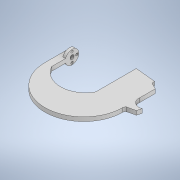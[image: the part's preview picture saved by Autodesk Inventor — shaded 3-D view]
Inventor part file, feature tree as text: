
AUTODESK INVENTOR PART (.ipt)
format: ipt  version: 2021 (Build 250183000, 183)  size: 172,032 bytes
history: native  units: in
note: dims shown in document units (in); Inventor stores cm internally (conversion verified against a paired STEP export)
features: other x3, extrude x3, sketch x3, projected_geometry x1
ambient origin geometry x8: Origin, YZ Plane, XZ Plane, XY Plane, X Axis, Y Axis, Z Axis, Center Point
bodies: Solid1 (feature_tree)
feature tree (10):
  other  "Blocks"
  extrude  "Extrusion1"  Depth=0.3937in
  extrude  "Extrusion2"  Depth=1.5748in
  extrude  "Extrusion3"  Depth=1.453in
  sketch  "Sketch1"  dims[d0=1.378in d1=0.3937in]
  sketch  "Sketch2"  dims[d2=2.3622in d3=1.5748in]
  other  "prindere"
  projected_geometry  "Projected Loop1"
  sketch  "Sketch3"  dims[d4=2.5591in d5=1.453in d6=0.4724in d7=0.1575in d8=0.2756in d9=0.4528in d10=1.1811in d11=0.4252in d12=0.1654in d13=0.455in d14=0.5788in d15=0.0478in d16=0.5278in d17=0.1072in d18=2.6386in d19=0.3106in d20=1.3542in d21=0.2362in d22=0.0in d23=0.1969in d24=0.1575in d25=0.0in d26=0.2362in d27=0.0in d28=0.0in]
  other  "prindere:1"
